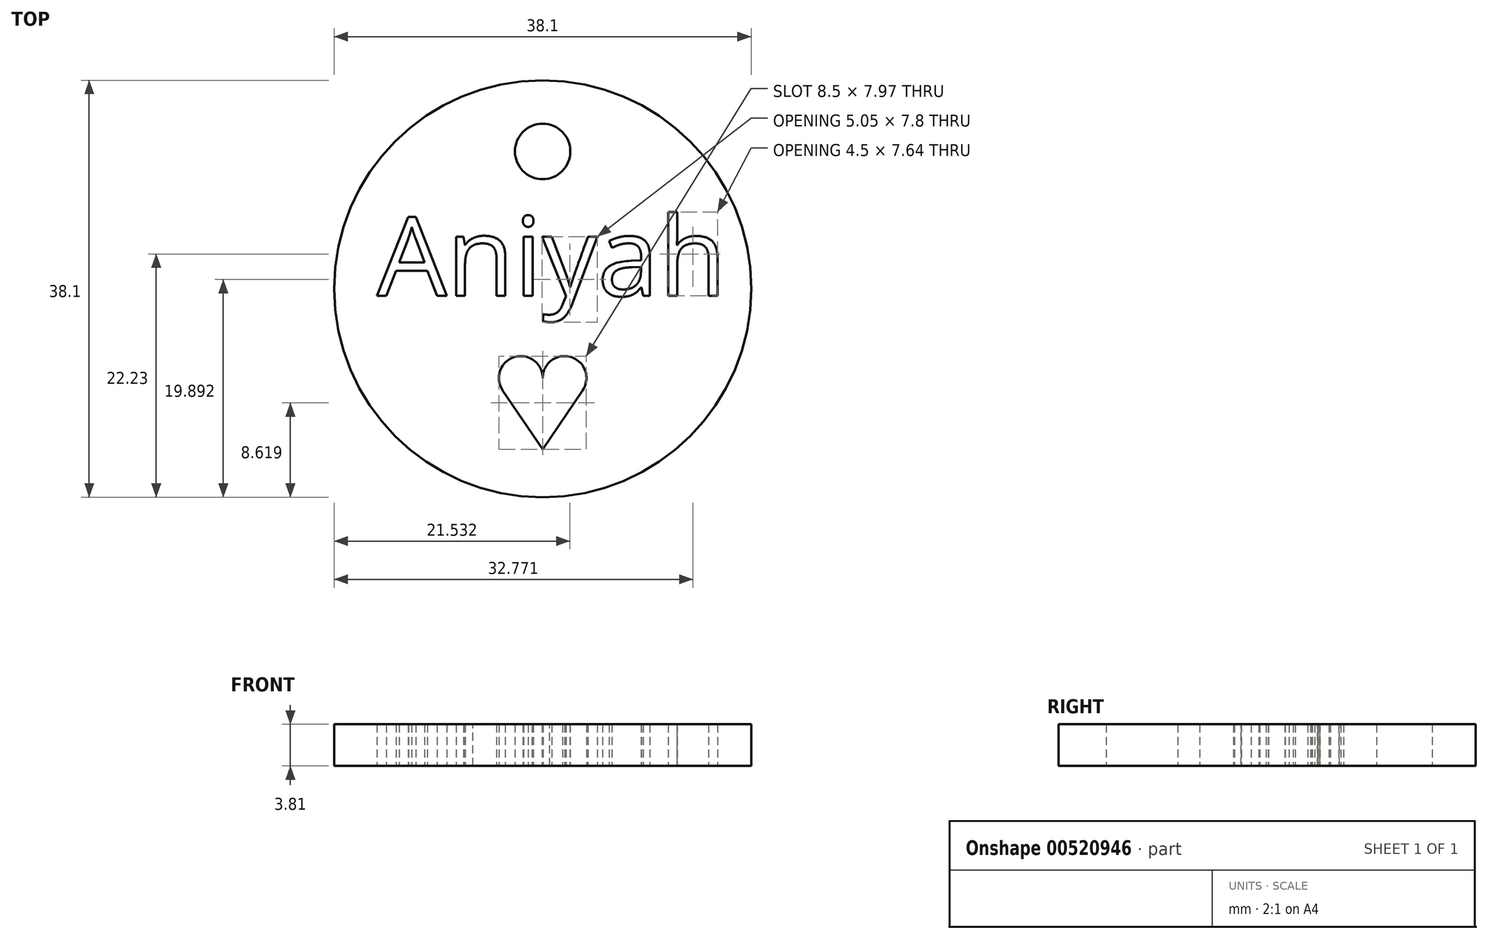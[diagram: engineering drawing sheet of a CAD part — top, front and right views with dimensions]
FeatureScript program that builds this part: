
annotation { "Feature Type Name" : "Feature", "Feature Type Description" : "" }
export const myFeature = defineFeature(function(context is Context, id is Id, definition is map)
    precondition{}
    {
        {
            var Q0;
            Q0=qCreatedBy(makeId("Top.planeOp"),FACE);
            var sketch = newSketch(context, id + "F0", { "sketchPlane" : qUnion([Q0])});
            skCircle(sketch, "E0", {"center": v(0, 0) * mm, "radius": 19.05 * mm});
            skSolve(sketch);
        }
        {
            var Q0;
            Q0 = qSketchRegion(id + "F0", true);
            extrude(context, id + "F1", {"entities" : qUnion([Q0]), "depth" : 3.81 * mm, "offsetDistance" : 25.4 * mm});
        }
        {
            var Q0;
            Q0=qCreatedBy(makeId("Top.planeOp"),FACE);
            var sketch = newSketch(context, id + "F2", { "sketchPlane" : qUnion([Q0])});
            skText(sketch, "E1", { "text": "Aniyah", "fontName": "OpenSans-Regular.ttf"});
            const initialGuessF2  = {"E1": [-0.01513, -0.00064, 1, 0, 0.00724]};
            skSetInitialGuess(sketch, initialGuessF2);
            skSolve(sketch);
        }
        {
            var Q0;
            Q0 = qSketchRegion(id + "F2", true);
            extrude(context, id + "F3", {"entities" : qUnion([Q0]), "operationType" : NewBodyOperationType.REMOVE, "depth" : 4 * mm, "offsetDistance" : 25.4 * mm});
        }
        {
            var Q0;
            Q0=qCreatedBy(makeId("Top.planeOp"),FACE);
            var sketch = newSketch(context, id + "F4", { "sketchPlane" : qUnion([Q0])});
            skCircle(sketch, "E2", {"center": v(0, 12.55) * mm, "radius": 2.53 * mm});
            skSolve(sketch);
        }
        {
            var Q0;
            Q0 = qSketchRegion(id + "F4", true);
            extrude(context, id + "F5", {"entities" : qUnion([Q0]), "operationType" : NewBodyOperationType.REMOVE, "depth" : 25.4 * mm, "offsetDistance" : 25.4 * mm});
        }
        {
            var Q0;
            Q0=qCreatedBy(makeId("Top.planeOp"),FACE);
            var sketch = newSketch(context, id + "F6", { "sketchPlane" : qUnion([Q0])});
            skCircle(sketch, "E3", {"center": v(-2, -8.15) * mm, "radius": 2 * mm});
            skLineSegment(sketch, "E4", {"start": v(0, -3.17) * mm, "end": v(0, -24.97) * mm});
            skCircle(sketch, "E5.MirrorC", {"center": v(2, -8.15) * mm, "radius": 2 * mm});
            skLineSegment(sketch, "E6", {"start": v(-3.66, -9.27) * mm, "end": v(0, -14.68) * mm});
            skLineSegment(sketch, "E7", {"start": v(0, -14.68) * mm, "end": v(3.66, -9.27) * mm});
            skSolve(sketch);
        }
        {
            var Q0;
            Q0 = qSketchRegion(id + "F6", true);
            extrude(context, id + "F7", {"entities" : qUnion([Q0]), "operationType" : NewBodyOperationType.REMOVE, "depth" : 25.4 * mm, "offsetDistance" : 25.4 * mm});
        }
    });
